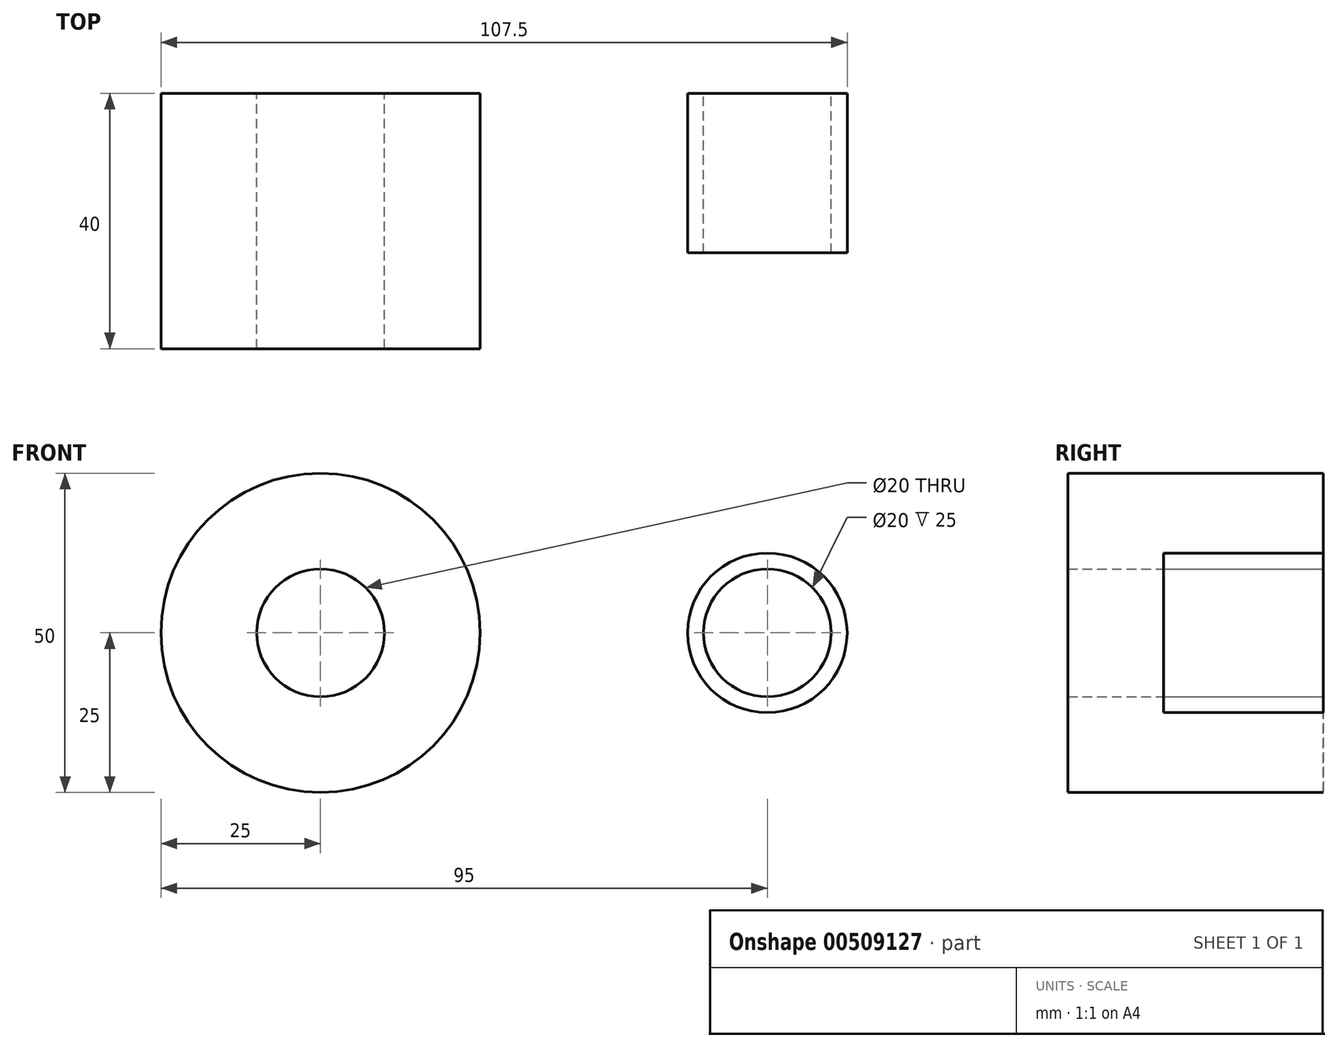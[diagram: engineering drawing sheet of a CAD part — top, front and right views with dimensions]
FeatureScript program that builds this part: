
annotation { "Feature Type Name" : "Feature", "Feature Type Description" : "" }
export const myFeature = defineFeature(function(context is Context, id is Id, definition is map)
    precondition{}
    {
        {
            var Q0;
            Q0=qCreatedBy(makeId("Front.planeOp"),FACE);
            var sketch = newSketch(context, id + "F0", { "sketchPlane" : qUnion([Q0])});
            skCircle(sketch, "E0", {"center": v(0, 0) * mm, "radius": 25 * mm});
            skCircle(sketch, "E1", {"center": v(70, 0) * mm, "radius": 12.5 * mm});
            skLineSegment(sketch, "E2", {"start": v(4.46, 24.6) * mm, "end": v(72.23, 12.3) * mm});
            skLineSegment(sketch, "E3", {"start": v(4.46, -24.6) * mm, "end": v(72.23, -12.3) * mm});
            skCircle(sketch, "E4", {"center": v(0, 0) * mm, "radius": 10 * mm});
            skCircle(sketch, "E5", {"center": v(70, 0) * mm, "radius": 10 * mm});
            skSolve(sketch);
        }
        {
            var Q0;
            {var subQ0=sQuery(id+"F0.wireOp",EDGE,"E2");Q0=makeQuery(id+"F0.imprint","IMPRINT",FACE,{"disambiguationData":[TD([[makeQuery(id+"F0.imprint","IMPRINT",EDGE,{"derivedFrom":subQ0}),-1.0]])]});}
            var sketch = newSketch(context, id + "F1", { "sketchPlane" : qUnion([Q0])});
            skSolve(sketch);
        }
        {
            var Q0;
            Q0=makeQuery(id+"F0.imprint","IMPRINT",FACE,{"disambiguationData":[TD([[makeQuery(id+"F0.imprint","IMPRINT",EDGE,{"derivedFrom":sQuery(id+"F0.wireOp",EDGE,"E5")}),-1.0]])]});
            var Q1;
            {var subQ0=sQuery(id+"F0.wireOp",EDGE,"E2");Q1=makeQuery(id+"F1.imprint","IMPRINT",FACE,{"disambiguationData":[TD([[makeQuery(id+"F1.imprint","IMPRINT",EDGE,{"derivedFrom":makeQuery(id+"F0.imprint","IMPRINT",EDGE,{"derivedFrom":subQ0})}),-1.0]])]});}
            extrude(context, id + "F2", {"entities" : qUnion([Q0, Q1]), "depth" : 25 * mm});
        }
        {
            var Q0;
            Q0=makeQuery(id+"F0.imprint","IMPRINT",FACE,{"disambiguationData":[TD([[makeQuery(id+"F0.imprint","IMPRINT",EDGE,{"derivedFrom":sQuery(id+"F0.wireOp",EDGE,"E4")}),-1.0]])]});
            extrude(context, id + "F3", {"entities" : qUnion([Q0]), "operationType" : NewBodyOperationType.ADD, "depth" : 40 * mm});
        }
    });
